# Revit family: ledlowbay-e_30w-4000-60d_545002000600
name_source: partatom
category: Leuchten
revit_build: Autodesk Revit 2016 (Build: 20190508_0715(x64)
units: mm (PartAtom-declared; Revit-internal decimal feet)

## family parameters
Basisbauteil = Fläche
Beim Laden mit Abzugskörper schneiden = Nein
Bemaßung runder Anschluss = Durchmesser verwenden
Gemeinsam genutzt = Nein
Lichtquelle = Nein
Raumberechnungspunkt = Nein
Teiletyp = Normal

## types (1)
- LEDLowbay-E 30W-4000-60D (1 x LED, 3000 lm)
    Approval mark = CE
    Beschreibung = Stylish solution for medium high ceilings in retail and industry.
    CIE Flux Codes = 73 98 100 100 100
    Control Gear = Electronic ballast
    Height = 1875 mm
    Hersteller = OPPLE
    Lamp Light Flux = 3000 lm
    Lamp count = 1
    Lampe = 1 x LED
    Length = 230 mm
    Luminous efficacy = 100 lm/W
    ModVariant = Nein
    Modell = 545002000600
    Mounting Place = Ceiling
    Mounting Type = Pendant
    Number of Poles = 1
    OnlyDefault = Ja
    Power Factor = 1
    Product Name = LEDLowbay-E 30W-4000-60D
    Product group = Lowbay
    ProductGroupID = 915
    Protection Class = Protection class I
    Protection Degree = IP 20
    RLX_Detail_Level = 1
    RlxData = <blob elided: 164937 chars, md5=e3049e74>
    Scheinlast = 30 VA
    Socket = socket
    Standby Power = 0 W
    System Light Flux = 3000 lm
    System Power = 30 W
    Typenbild = 545002000600.jpg
    Typenkommentare = Product without accessories
    URL = http://relux.com
    VarID = ---
    Voltage = 0 V
    Vorgabe-Ansicht = 1800 mm
    Weight = 0.00 kg
    Width = 0 mm  [stored 0 ft]

note: [stored X ft] marks values corroborated as IEEE doubles in the binary element streams (Revit-internal decimal feet)

## geometry (parser evidence)
native form markers: Blend x4, Sweep x11
no freeform markers — native parametric forms only
